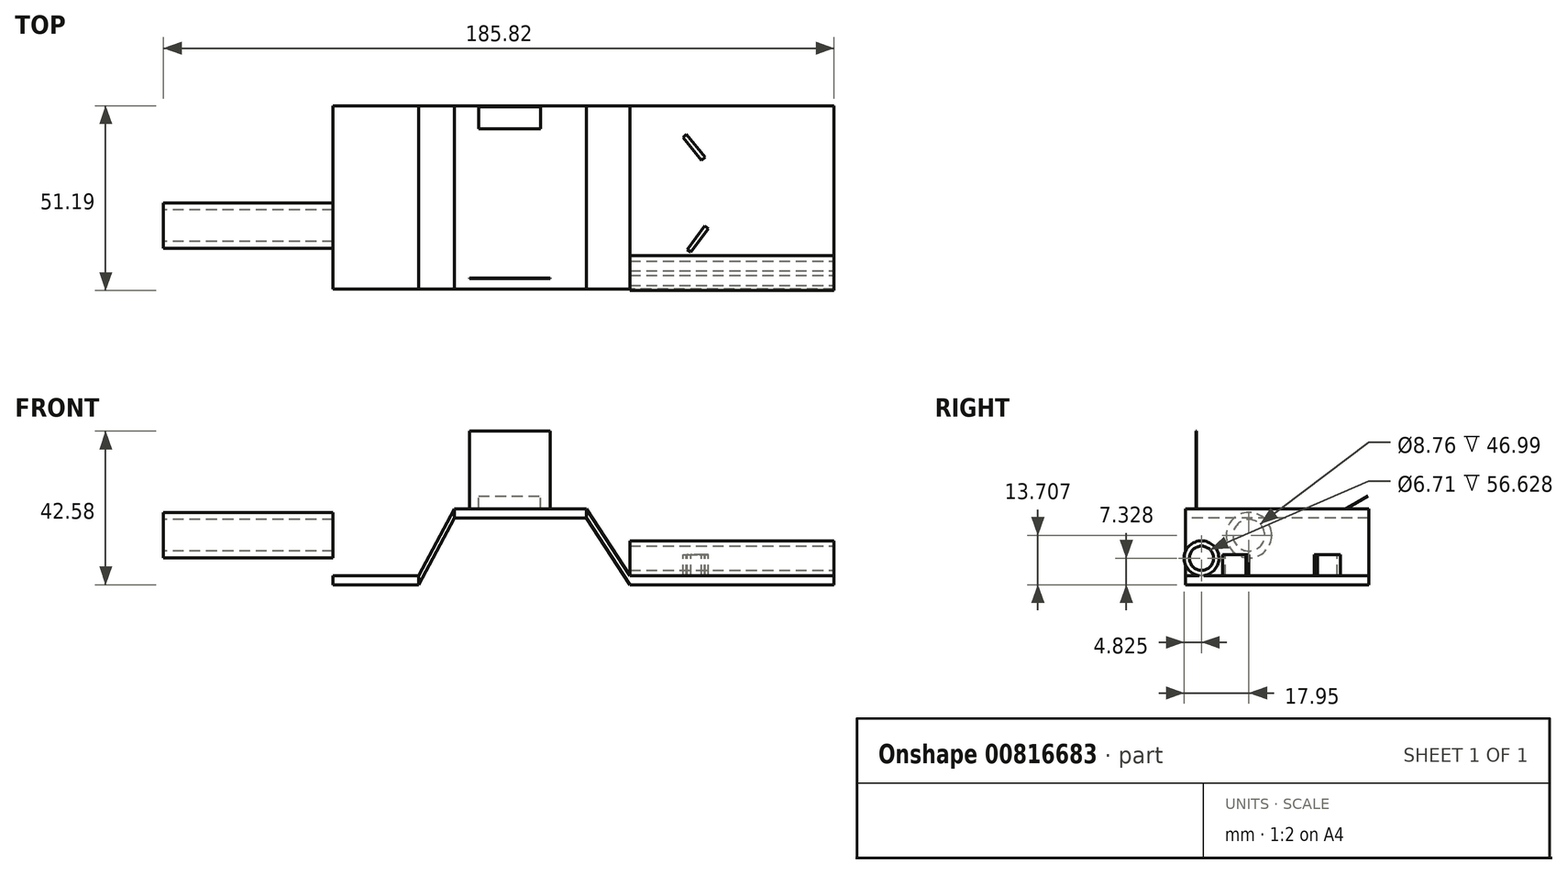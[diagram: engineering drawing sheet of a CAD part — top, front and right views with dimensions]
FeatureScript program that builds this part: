
annotation { "Feature Type Name" : "Feature", "Feature Type Description" : "" }
export const myFeature = defineFeature(function(context is Context, id is Id, definition is map)
    precondition{}
    {
        {
            var Q0;
            Q0=qCreatedBy(makeId("Front.planeOp"),FACE);
            var sketch = newSketch(context, id + "F0", { "sketchPlane" : qUnion([Q0])});
            skLineSegment(sketch, "E0", {"start": v(75.44, 0) * mm, "end": v(18.82, 0) * mm});
            skLineSegment(sketch, "E1", {"start": v(18.82, 0) * mm, "end": v(6.76, 18.45) * mm});
            skLineSegment(sketch, "E2", {"start": v(6.76, 18.45) * mm, "end": v(-29.78, 18.45) * mm});
            skLineSegment(sketch, "E3", {"start": v(-29.78, 18.45) * mm, "end": v(-39.64, 0) * mm});
            skLineSegment(sketch, "E4", {"start": v(-39.64, 0) * mm, "end": v(-63.39, 0) * mm});
            skSolve(sketch);
        }
        {
            var Q0;
            Q0 = qSketchRegion(id + "F0", true);
            var Q1;
            Q1=sQuery(id+"F0.wireOp",EDGE,"E0");
            var Q2;
            Q2=sQuery(id+"F0.wireOp",EDGE,"E1");
            var Q3;
            Q3=sQuery(id+"F0.wireOp",EDGE,"E2");
            var Q4;
            Q4=sQuery(id+"F0.wireOp",EDGE,"E3");
            var Q5;
            Q5=sQuery(id+"F0.wireOp",EDGE,"E4");
            extrude(context, id + "F1", {"entities" : qUnion([Q0]), "bodyType" : ToolBodyType.SURFACE, "surfaceEntities" : qUnion([Q1, Q2, Q3, Q4, Q5]), "endBound" : BoundingType.SYMMETRIC, "depth" : 50.8 * mm, "offsetDistance" : 25.4 * mm});
        }
        {
            var Q0;
            Q0=makeQuery(id+"F1.opExtrude","SWEPT_FACE",FACE,{"disambiguationData":[OSD([sQuery(id+"F0.wireOp",EDGE,"E0")])]});
            var sketch = newSketch(context, id + "F2", { "sketchPlane" : qUnion([Q0])});
            skLineSegment(sketch, "E5", {"start": v(34.52, 17.48) * mm, "end": v(39.64, 11.14) * mm});
            skLineSegment(sketch, "E6", {"start": v(40.61, -8.59) * mm, "end": v(35.74, -15.16) * mm});
            skSolve(sketch);
        }
        {
            var Q0;
            Q0=makeQuery(id+"F2.imprint","IMPRINT",FACE,{"disambiguationData":[TD([[makeQuery(id+"F2.imprint","IMPRINT",EDGE,{"derivedFrom":makeQuery(id+"F1.opExtrude","SWEPT_EDGE",EDGE,{"disambiguationData":[OSD([sQuery(id+"F0.wireOp",VERTEX,"E0.start")])]})}),-1.0]])]});
            var Q1;
            Q1=makeQuery(id+"F1.opExtrude","SWEPT_FACE",FACE,{"disambiguationData":[OSD([sQuery(id+"F0.wireOp",EDGE,"E1")])]});
            var Q2;
            Q2=makeQuery(id+"F1.opExtrude","SWEPT_FACE",FACE,{"disambiguationData":[OSD([sQuery(id+"F0.wireOp",EDGE,"E2")])]});
            var Q3;
            Q3=makeQuery(id+"F1.opExtrude","SWEPT_FACE",FACE,{"disambiguationData":[OSD([sQuery(id+"F0.wireOp",EDGE,"E3")])]});
            var Q4;
            Q4=makeQuery(id+"F1.opExtrude","SWEPT_FACE",FACE,{"disambiguationData":[OSD([sQuery(id+"F0.wireOp",EDGE,"E4")])]});
            extrude(context, id + "F3", {"entities" : qUnion([Q0, Q1, Q2, Q3, Q4]), "oppositeDirection" : true, "depth" : 2.54 * mm, "offsetDistance" : 25.4 * mm});
        }
        {
            var Q0;
            Q0 = qSketchRegion(id + "F2", true);
            var Q1;
            Q1 = qConstructionFilter(qBodyType(qCreatedBy(id + "F2" ,EDGE), BodyType.WIRE), ConstructionObject.NO);
            extrude(context, id + "F4", {"entities" : qUnion([Q0]), "bodyType" : ToolBodyType.SURFACE, "surfaceEntities" : qUnion([Q1]), "depth" : 5.84 * mm, "offsetDistance" : 25.4 * mm});
        }
        {
            var Q0;
            Q0=makeQuery(id+"F4.opExtrude","SWEPT_FACE",FACE,{"disambiguationData":[OSD([sQuery(id+"F2.wireOp",EDGE,"E6")])]});
            extrude(context, id + "F5", {"entities" : qUnion([Q0]), "operationType" : NewBodyOperationType.ADD, "depth" : 1.27 * mm, "offsetDistance" : 25.4 * mm});
        }
        {
            var Q0;
            Q0=makeQuery(id+"F4.opExtrude","SWEPT_FACE",FACE,{"disambiguationData":[OSD([sQuery(id+"F2.wireOp",EDGE,"E5")])]});
            extrude(context, id + "F6", {"entities" : qUnion([Q0]), "operationType" : NewBodyOperationType.ADD, "depth" : 1.27 * mm, "offsetDistance" : 25.4 * mm});
        }
        {
            var Q0;
            Q0=makeQuery(id+"F1.opExtrude","SWEPT_FACE",FACE,{"disambiguationData":[OSD([sQuery(id+"F0.wireOp",EDGE,"E2")])]});
            var sketch = newSketch(context, id + "F7", { "sketchPlane" : qUnion([Q0])});
            skLineSegment(sketch, "E7", {"start": v(-24.7, 22.06) * mm, "end": v(-2.35, 22.06) * mm});
            skLineSegment(sketch, "E8", {"start": v(-25.59, -22.5) * mm, "end": v(-3.23, -22.5) * mm});
            skSolve(sketch);
        }
        {
            assignVariable(context, id + "F8", {"name" : "plate_thickness", "anyValue" : 0.1});
        }
        {
            assignVariable(context, id + "F9", {"name" : "thick", "anyValue" : 21.59 * mm});
        }
        {
            var Q0;
            Q0=sQuery(id+"F7.wireOp",EDGE,"E8");
            extrude(context, id + "F10", {"bodyType" : ToolBodyType.SURFACE, "surfaceEntities" : qUnion([Q0]), "depth" : (getVariable(context, 'thick')), "offsetDistance" : 25.4 * mm});
        }
        {
            var Q0;
            Q0=makeQuery(id+"F10.opExtrude","SWEPT_FACE",FACE,{"disambiguationData":[OSD([sQuery(id+"F7.wireOp",EDGE,"E8")])]});
            extrude(context, id + "F11", {"entities" : qUnion([Q0]), "oppositeDirection" : true, "depth" : (getVariable(context, 'plate_thickness')) * mm, "offsetDistance" : 25.4 * mm});
        }
        {
            var Q0;
            {var subQ0=sQuery(id+"F0.wireOp",EDGE,"E0");var subQ1=sQuery(id+"F0.wireOp",VERTEX,"E0.start");Q0=makeQuery(id+"F3.opExtrude","CAP_VERTEX",VERTEX,{"disambiguationData":[OSD([subQ1,subQ0]),TDD([makeQuery(id+"F2.imprint","INTERSECT",VERTEX,{"derivedFrom":[makeQuery(id+"F1.opExtrude","SWEPT_EDGE",EDGE,{"disambiguationData":[OSD([subQ1])]}),makeQuery(id+"F1.opExtrude","CAP_EDGE",EDGE,{"disambiguationData":[OSD([subQ0])],"isStart":false})]})])],"isStart":true});}
            var Q1;
            {var subQ0=sQuery(id+"F0.wireOp",EDGE,"E0");var subQ1=sQuery(id+"F0.wireOp",VERTEX,"E0.start");Q1=makeQuery(id+"F3.opExtrude","CAP_VERTEX",VERTEX,{"disambiguationData":[OSD([subQ1,subQ0]),TDD([makeQuery(id+"F2.imprint","INTERSECT",VERTEX,{"derivedFrom":[makeQuery(id+"F1.opExtrude","SWEPT_EDGE",EDGE,{"disambiguationData":[OSD([subQ1])]}),makeQuery(id+"F1.opExtrude","CAP_EDGE",EDGE,{"disambiguationData":[OSD([subQ0])],"isStart":false})]})])],"isStart":false});}
            var Q2;
            {var subQ0=sQuery(id+"F0.wireOp",EDGE,"E0");var subQ1=sQuery(id+"F0.wireOp",VERTEX,"E0.start");Q2=makeQuery(id+"F3.opExtrude","CAP_VERTEX",VERTEX,{"disambiguationData":[OSD([subQ1,subQ0]),TDD([makeQuery(id+"F2.imprint","INTERSECT",VERTEX,{"derivedFrom":[makeQuery(id+"F1.opExtrude","SWEPT_EDGE",EDGE,{"disambiguationData":[OSD([subQ1])]}),makeQuery(id+"F1.opExtrude","CAP_EDGE",EDGE,{"disambiguationData":[OSD([subQ0])],"isStart":true})]})])],"isStart":true});}
            cPlane(context, id + "F12", {"entities" : qUnion([Q0, Q1, Q2]), "cplaneType" : CPlaneType.THREE_POINT, "offset" : 0 * mm, "width" : 152.4 * mm, "height" : 152.4 * mm});
        }
        {
            var Q0;
            Q0=qCreatedBy(id+"F12.planeOp",FACE);
            var sketch = newSketch(context, id + "F13", { "sketchPlane" : qUnion([Q0])});
            skCircle(sketch, "E9", {"center": v(20.97, 4.79) * mm, "radius": 4.83 * mm});
            skCircle(sketch, "E10", {"center": v(20.97, 4.79) * mm, "radius": 3.36 * mm});
            skSolve(sketch);
        }
        {
            var Q0;
            Q0=makeQuery(id+"F13.imprint","IMPRINT",FACE,{"disambiguationData":[TD([[makeQuery(id+"F13.imprint","IMPRINT",EDGE,{"derivedFrom":sQuery(id+"F13.wireOp",EDGE,"E9")}),1.0]])]});
            var Q1;
            {var subQ0=sQuery(id+"F0.wireOp",VERTEX,"E1.start");Q1=makeQuery(id+"F3.opExtrude","SWEPT_FACE",FACE,{"disambiguationData":[OSD([subQ0]),TDD([makeQuery(id+"F2.imprint","IMPRINT",EDGE,{"derivedFrom":makeQuery(id+"F1.opExtrude","SWEPT_EDGE",EDGE,{"disambiguationData":[OSD([subQ0])]})})])]});}
            extrude(context, id + "F14", {"entities" : qUnion([Q0]), "operationType" : NewBodyOperationType.ADD, "endBound" : BoundingType.UP_TO_SURFACE, "depth" : 25.4 * mm, "endBoundEntityFace" : qUnion([Q1]), "offsetDistance" : 25.4 * mm});
        }
        {
            var Q0;
            Q0=makeQuery(id+"F3.opExtrude","CAP_FACE",FACE,{"disambiguationData":[OSD([sQuery(id+"F0.wireOp",EDGE,"E2")])],"isStart":true});
            var sketch = newSketch(context, id + "F15", { "sketchPlane" : qUnion([Q0])});
            skLineSegment(sketch, "E11", {"start": v(-22.7, 18.85) * mm, "end": v(-5.81, 18.85) * mm});
            skSolve(sketch);
        }
        {
            var Q0;
            Q0=sQuery(id+"F15.wireOp",EDGE,"E11");
            cPlane(context, id + "F16", {"entities" : qUnion([Q0]), "cplaneType" : CPlaneType.LINE_ANGLE, "offset" : 25.4 * mm, "angle" : 120 * degree, "width" : 152.4 * mm, "height" : 152.4 * mm});
        }
        {
            var Q0;
            Q0=qCreatedBy(id+"F16.planeOp",FACE);
            var sketch = newSketch(context, id + "F17", { "sketchPlane" : qUnion([Q0])});
            skLineSegment(sketch, "E12.bottom", {"start": v(-23.06, 25.78) * mm, "end": v(-5.93, 25.78) * mm});
            skLineSegment(sketch, "E12.top", {"start": v(-23.06, 32.81) * mm, "end": v(-5.93, 32.81) * mm});
            skLineSegment(sketch, "E12.left", {"start": v(-23.06, 25.78) * mm, "end": v(-23.06, 32.81) * mm});
            skLineSegment(sketch, "E12.right", {"start": v(-5.93, 25.78) * mm, "end": v(-5.93, 32.81) * mm});
            skSolve(sketch);
        }
        {
            var Q0;
            Q0 = qSketchRegion(id + "F17", true);
            extrude(context, id + "F18", {"entities" : qUnion([Q0]), "oppositeDirection" : true, "depth" : (getVariable(context, 'plate_thickness')) * mm, "offsetDistance" : 25.4 * mm});
        }
        {
            var Q0;
            {var subQ0=sQuery(id+"F0.wireOp",VERTEX,"E4.end");Q0=makeQuery(id+"F3.opExtrude","CAP_VERTEX",VERTEX,{"disambiguationData":[OSD([subQ0]),TDD([makeQuery(id+"F1.opExtrude","CAP_VERTEX",VERTEX,{"disambiguationData":[OSD([subQ0])],"isStart":true})])],"isStart":true});}
            var Q1;
            {var subQ0=sQuery(id+"F0.wireOp",VERTEX,"E4.end");Q1=makeQuery(id+"F3.opExtrude","CAP_VERTEX",VERTEX,{"disambiguationData":[OSD([subQ0]),TDD([makeQuery(id+"F1.opExtrude","CAP_VERTEX",VERTEX,{"disambiguationData":[OSD([subQ0])],"isStart":false})])],"isStart":false});}
            var Q2;
            {var subQ0=sQuery(id+"F0.wireOp",VERTEX,"E4.end");Q2=makeQuery(id+"F3.opExtrude","CAP_VERTEX",VERTEX,{"disambiguationData":[OSD([subQ0]),TDD([makeQuery(id+"F1.opExtrude","CAP_VERTEX",VERTEX,{"disambiguationData":[OSD([subQ0])],"isStart":false})])],"isStart":true});}
            cPlane(context, id + "F19", {"entities" : qUnion([Q0, Q1, Q2]), "cplaneType" : CPlaneType.THREE_POINT, "offset" : 25.4 * mm, "width" : 152.4 * mm, "height" : 152.4 * mm});
        }
        {
            var Q0;
            Q0=qCreatedBy(id+"F19.planeOp",FACE);
            cPlane(context, id + "F20", {"entities" : qUnion([Q0]), "cplaneType" : CPlaneType.OFFSET, "offset" : 47 * mm, "oppositeDirection" : true, "width" : 152.4 * mm, "height" : 152.4 * mm});
        }
        {
            var Q0;
            Q0=qCreatedBy(id+"F20.planeOp",FACE);
            var sketch = newSketch(context, id + "F21", { "sketchPlane" : qUnion([Q0])});
            skLineSegment(sketch, "E13", {"start": v(-46.53, 0) * mm, "end": v(31.15, 0) * mm});
            skLineSegment(sketch, "E14.bottom", {"start": v(10.32, 0) * mm, "end": v(-22.51, 0) * mm});
            skLineSegment(sketch, "E14.top", {"start": v(10.32, 21.85) * mm, "end": v(-22.51, 21.85) * mm});
            skLineSegment(sketch, "E14.left", {"start": v(10.32, 0) * mm, "end": v(10.32, 21.85) * mm});
            skLineSegment(sketch, "E14.right", {"start": v(-22.51, 0) * mm, "end": v(-22.51, 21.85) * mm});
            skCircle(sketch, "E15", {"center": v(-7.84, 11.17) * mm, "radius": 6.3 * mm});
            skCircle(sketch, "E16", {"center": v(-7.84, 11.17) * mm, "radius": 4.38 * mm});
            skSolve(sketch);
        }
        {
            var Q0;
            Q0=makeQuery(id+"F21.imprint","IMPRINT",FACE,{"disambiguationData":[TD([[makeQuery(id+"F21.imprint","IMPRINT",EDGE,{"derivedFrom":sQuery(id+"F21.wireOp",EDGE,"E15")}),1.0]])]});
            var Q1;
            Q1=qCreatedBy(id+"F19.planeOp",FACE);
            extrude(context, id + "F22", {"entities" : qUnion([Q0]), "endBound" : BoundingType.UP_TO_SURFACE, "depth" : 28.2 * mm, "endBoundEntityFace" : qUnion([Q1]), "offsetDistance" : 25.4 * mm});
        }
    });
